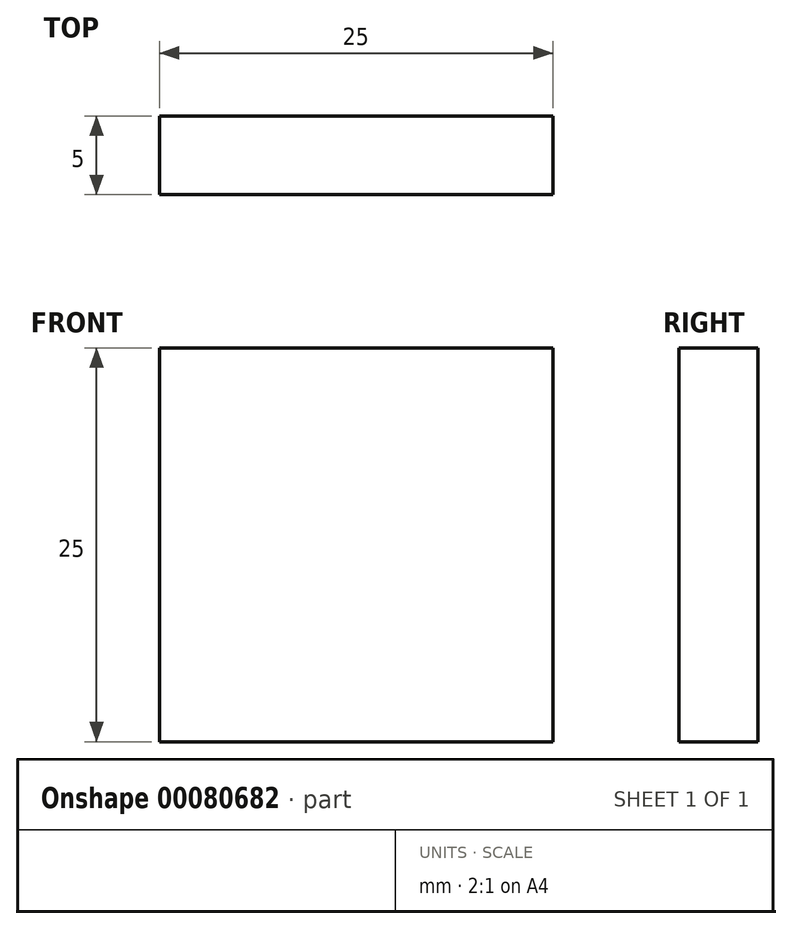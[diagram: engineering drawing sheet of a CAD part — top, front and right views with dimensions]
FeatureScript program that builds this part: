
annotation { "Feature Type Name" : "Feature", "Feature Type Description" : "" }
export const myFeature = defineFeature(function(context is Context, id is Id, definition is map)
    precondition{}
    {
        {
            var Q0;
            Q0=qCreatedBy(makeId("Front.planeOp"),FACE);
            var sketch = newSketch(context, id + "F0", { "sketchPlane" : qUnion([Q0])});
            skLineSegment(sketch, "E0.bottom", {"start": v(12.5, 12.5) * mm, "end": v(-12.5, 12.5) * mm});
            skLineSegment(sketch, "E0.top", {"start": v(12.5, -12.5) * mm, "end": v(-12.5, -12.5) * mm});
            skLineSegment(sketch, "E0.left", {"start": v(12.5, 12.5) * mm, "end": v(12.5, -12.5) * mm});
            skLineSegment(sketch, "E0.right", {"start": v(-12.5, 12.5) * mm, "end": v(-12.5, -12.5) * mm});
            skPoint(sketch, "E0.middle", {"position": v(0, 0) * mm});
            skSolve(sketch);
        }
        {
            var Q0;
            Q0=makeQuery(id+"F0.imprint","IMPRINT",FACE,{"disambiguationData":[TD([[makeQuery(id+"F0.imprint","IMPRINT",EDGE,{"derivedFrom":sQuery(id+"F0.wireOp",EDGE,"E0.bottom")}),1.0]])]});
            extrude(context, id + "F1", {"entities" : qUnion([Q0]), "depth" : 5 * mm});
        }
    });
